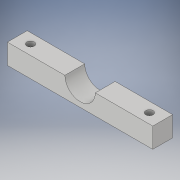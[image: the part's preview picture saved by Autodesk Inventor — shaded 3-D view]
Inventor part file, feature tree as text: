
AUTODESK INVENTOR PART (.ipt)
format: ipt  version: 2019.4 (Build 234330000, 330)  size: 117,760 bytes
history: native  units: in
note: dims shown in document units (in); Inventor stores cm internally (conversion verified against a paired STEP export)
features: sketch x3, extrude x2, hole x1
ambient origin geometry x8: Origin, YZ Plane, XZ Plane, XY Plane, X Axis, Y Axis, Z Axis, Center Point
bodies: Solid1 (feature_tree)
feature tree (6):
  extrude  "Extrusion1"  Depth=0.75in
  extrude  "Extrusion2"  Depth=0.7625in
  hole  "Hole1"  [1 undecoded]
  sketch  "Sketch1"  dims[d0=5.5in d1=0.75in]
  sketch  "Sketch2"  dims[d2=0.7625in d3=0.0in d4=1.15in]
  sketch  "Sketch3"  dims[d5=1.0in d6=0.0in d7=0.375in d8=0.5in d13=0.375in d14=0.5in d15=0.281in d16=0.75in d17=0.75in d18=0.188in d19=0.5635in d20=1.0in d21=0.0in]
note: 1 required parameter value undecoded (feature->parameter linkage not recoverable at this tier; creation-order binding heuristic only, values carry confidence <= 0.55)
